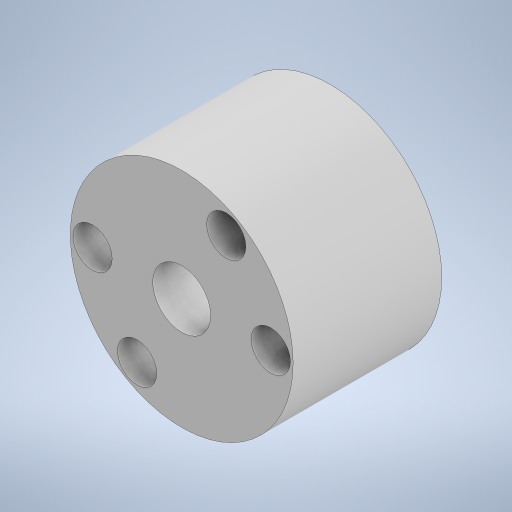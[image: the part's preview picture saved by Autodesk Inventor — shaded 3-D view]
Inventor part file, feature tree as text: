
AUTODESK INVENTOR PART (.ipt)
format: ipt  version: 2023 (Build 270158000, 158)  size: 245,760 bytes
history: native  units: in
note: dims shown in document units (in); Inventor stores cm internally (conversion verified against a paired STEP export)
features: extrude x1, sketch x1
ambient origin geometry x8: Origin, YZ Plane, XZ Plane, XY Plane, X Axis, Y Axis, Z Axis, Center Point
bodies: Body1 (feature_tree)
feature tree (2):
  extrude  "Extrusion14"  Depth=0.5in
  sketch  "Sketch1"  dims[d3=0.866in d15=0.75in d37=0.75in d69=0.132in d70=0.132in d73=0.5in d74=0.0in d75=0.132in d76=0.132in d79=0.3in d80=0.3in d82=0.195in d83=0.3in d84=0.3in d85=0.5in d86=0.0344in d87=0.5in d88=0.0344in]
